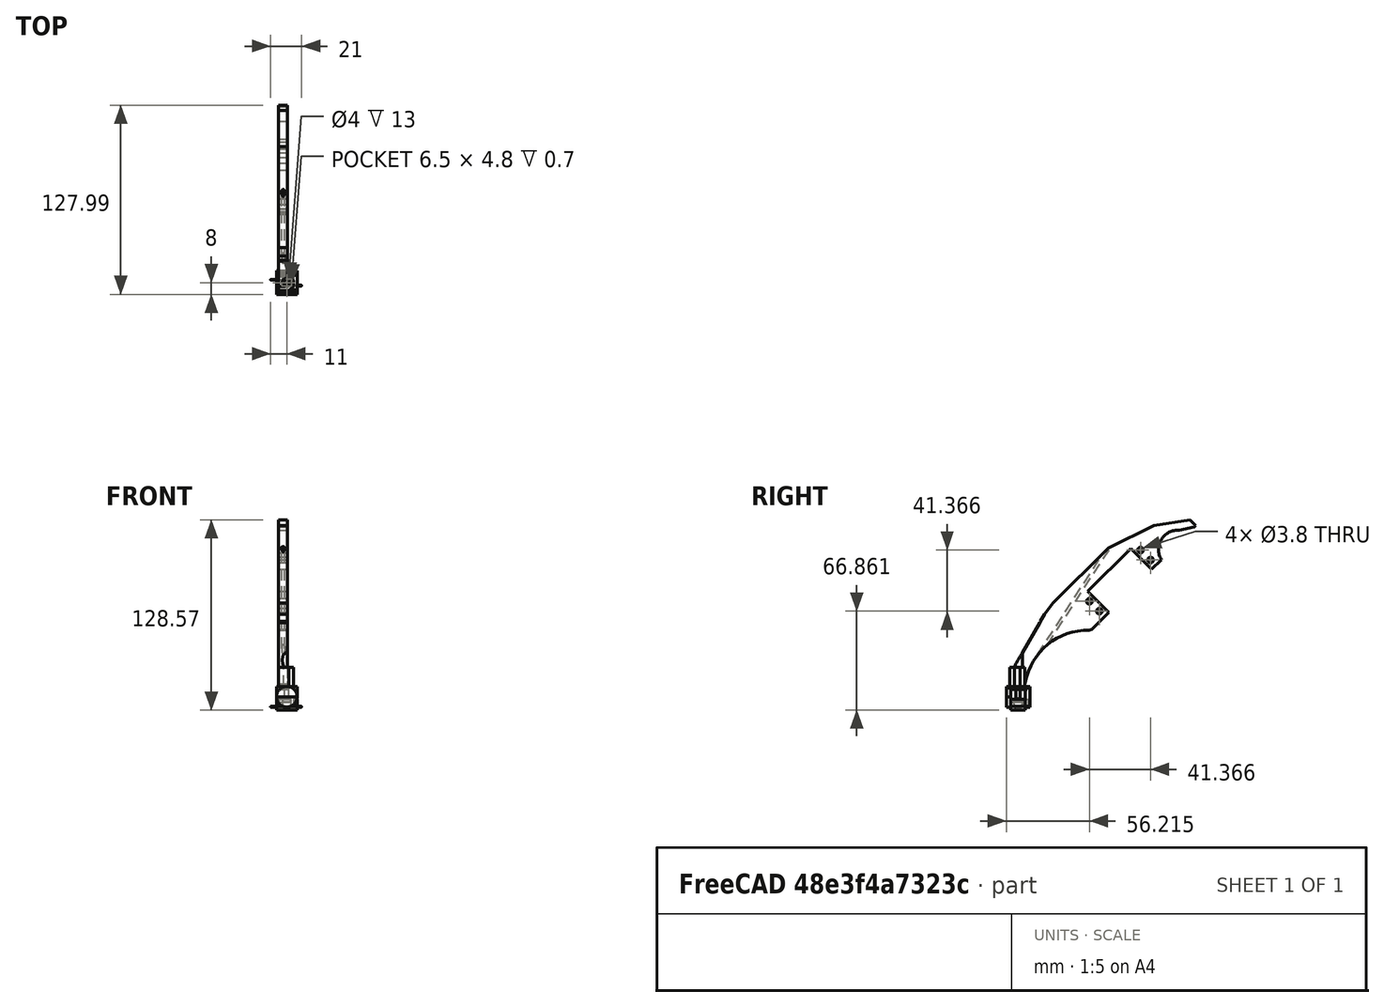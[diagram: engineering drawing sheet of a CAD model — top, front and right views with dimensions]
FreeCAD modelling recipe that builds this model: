
FCSTD DOCUMENT  (FreeCAD 0.16R6710 (Git))
Label: Leg and feet sensors 0.1
License: All rights reserved
LicenseURL: http://en.wikipedia.org/wiki/All_rights_reserved
objects: Part::Cut×27, Part::Box×24, Part::Cylinder×18, Part::Fuse×8, Part::Chamfer×4, Part::Sphere×2, Part::Fillet×2, Part::MultiCommon×1
note: 86 computed .brp shape members not serialized (recipe doc carries the construction recipe); baked Part::Feature solids carry a one-line shape summary decoded from their .brp

FEATURE [Part::Sphere] Sphere
  Angle1 = -90
  Angle2 = 90
  Angle3 = 360
  Radius = 3
FEATURE [Part::Cylinder] Cylinder
  Angle = 360
  Height = 10
  Radius = 1.5
FEATURE [Part::Box] Box  label="Cube"
  Height = 1
  Length = 6.5
  Placement = pos=(-3.25,-2.4,-4.2) rot=(0,0,1;0rad)
  Width = 4.8
FEATURE [Part::Cylinder] Cylinder001
  Angle = 360
  Height = 10
  Placement = pos=(-11,2,-3.7) rot=(0,1,0;1.5708rad)
  Radius = 0.25
FEATURE [Part::Cylinder] Cylinder002
  Angle = 360
  Height = 10
  Placement = pos=(0,-2,-3.7) rot=(0,1,0;1.5708rad)
  Radius = 0.25
FEATURE [Part::Box] Box001  label="Cube001"
  Height = 7.25
  Length = 14
  Placement = pos=(-7,-5,-6) rot=(0,0,1;0rad)
  Width = 10
FEATURE [Part::Box] Box002  label="Cube002"
  Height = 1
  Length = 6.5
  Placement = pos=(-3.25,-2.4,-4.2) rot=(0,0,1;0rad)
  Width = 4.8
FEATURE [Part::Cylinder] Cylinder003
  Angle = 360
  Height = 10
  Placement = pos=(-11,2,-3.7) rot=(0,1,0;1.5708rad)
  Radius = 0.25
FEATURE [Part::Cylinder] Cylinder004
  Angle = 360
  Height = 10
  Placement = pos=(0,-2,-3.7) rot=(0,1,0;1.5708rad)
  Radius = 0.25
FEATURE [Part::Fuse] Fusion
  Base = -> Cylinder003
  Tool = -> Cylinder004
FEATURE [Part::Fuse] Fusion001
  Base = -> Box002
  Tool = -> Fusion
FEATURE [Part::Box] Box003  label="Cube003"
  Height = 3
  Length = 10
  Placement = pos=(-5,-6,-3.5) rot=(0,0,1;0rad)
  Width = 12
FEATURE [Part::Cut] Cut
  Base = -> Box001
  Tool = -> Box003
FEATURE [Part::Cut] Cut001
  Base = -> Cut
  Tool = -> Fusion001
FEATURE [Part::Fuse] Fusion002
  Base = -> Cylinder001
  Tool = -> Cylinder002
FEATURE [Part::Fuse] Fusion003  label="Switch"
  Base = -> Box
  Tool = -> Fusion002
FEATURE [Part::Box] Box004  label="Cube004"
  Height = 5
  Length = 10
  Placement = pos=(-5,4,-3.55) rot=(0,0,1;0rad)
  Width = 3
FEATURE [Part::Sphere] Sphere001
  Angle1 = -90
  Angle2 = 90
  Angle3 = 360
  Radius = 3.1
FEATURE [Part::Cylinder] Cylinder005
  Angle = 360
  Height = 10
  Placement = pos=(0,0,0.5) rot=(0,0,1;0rad)
  Radius = 2.5
FEATURE [Part::Fuse] Fusion004
  Base = -> Sphere001
  Tool = -> Cylinder005
FEATURE [Part::Cut] Cut002
  Base = -> Cut001
  Tool = -> Fusion004
FEATURE [Part::Fuse] Fusion005  label="Ball and Screw"
  Base = -> Sphere
  Placement = pos=(0,0,-1) rot=(0,0,1;0rad)
  Tool = -> Cylinder
FEATURE [Part::Cut] Cut003
  Base = -> Cut001
  Tool = -> Fusion004
FEATURE [Part::Box] Box005  label="Cube005"
  Height = 8
  Length = 21
  Placement = pos=(-9,-7,-3.5) rot=(0,0,1;0rad)
  Width = 17
FEATURE [Part::Box] Box006  label="Cube006"
  Height = 12
  Length = 21
  Placement = pos=(-9,-7,-3.5) rot=(0,0,1;0rad)
  Width = 17
FEATURE [Part::Cut] Cut004  label="Bottom Switch holder"
  Base = -> Cut003
  Tool = -> Box005
FEATURE [Part::MultiCommon] Common  label="Ball and screw holder"
  Shapes = -> [Cut002,Box006]
FEATURE [Part::Box] Box007  label="Cube007"
  Height = 7
  Length = 14
  Placement = pos=(-7,5,3) rot=(0,0,1;0rad)
  Width = 3
FEATURE [Part::Cylinder] Cylinder006
  Angle = 360
  Height = 3
  Placement = pos=(0,8,3) rot=(1,0,0;1.5708rad)
  Radius = 7
FEATURE [Part::Fuse] Fusion006
  Base = -> Box007
  Tool = -> Cylinder006
FEATURE [Part::Box] Box008  label="Cube008"
  Height = 7
  Length = 14
  Placement = pos=(-7,-8,3) rot=(0,0,1;0rad)
  Width = 3
FEATURE [Part::Cylinder] Cylinder007
  Angle = 360
  Height = 3
  Placement = pos=(0,-5,3) rot=(1,0,0;1.5708rad)
  Radius = 7
FEATURE [Part::Box] Box009  label="Cube009"
  Height = 2
  Length = 14
  Placement = pos=(-7,-6,8) rot=(0,0,1;0rad)
  Width = 12
FEATURE [Part::Box] Box010  label="Cube010"
  Height = 12
  Length = 41
  Placement = pos=(42,14,-1) rot=(0,0,1;0rad)
  Width = 20
FEATURE [Part::Cylinder] Cylinder011
  Angle = 360
  Height = 12
  Placement = pos=(38,19.5,-1) rot=(0,0,1;0rad)
  Radius = 1.9
FEATURE [Part::Cylinder] Cylinder012
  Angle = 360
  Height = 12
  Placement = pos=(38,29,-1) rot=(0,0,1;0rad)
  Radius = 1.9
FEATURE [Part::Cylinder] Cylinder013
  Angle = 360
  Height = 12
  Placement = pos=(87,29,-1) rot=(0,0,1;0rad)
  Radius = 1.9
FEATURE [Part::Cylinder] Cylinder014
  Angle = 360
  Height = 12
  Placement = pos=(87,19.5,-1) rot=(0,0,1;0rad)
  Radius = 1.9
FEATURE [Part::Box] Box011  label="Cube011"
  Height = 6
  Length = 184
  Width = 34
FEATURE [Part::Box] Box012  label="Cube012"
  Height = 12
  Length = 37
  Width = 8
FEATURE [Part::Cylinder] Cylinder015
  Angle = 360
  Height = 10
  Placement = pos=(20,37,0) rot=(0,0,1;0rad)
  Radius = 13
FEATURE [Part::Cut] Cut008
  Base = -> Box011
  Tool = -> Box012
FEATURE [Part::Cut] Cut009
  Base = -> Cut008
  Tool = -> Cylinder015
FEATURE [Part::Cylinder] Cylinder016
  Angle = 360
  Height = 10
  Placement = pos=(132,63,0) rot=(0,0,1;0rad)
  Radius = 43
FEATURE [Part::Cut] Cut010
  Base = -> Cut009
  Tool = -> Cylinder016
FEATURE [Part::Box] Box013  label="Cube013"
  Height = 10
  Length = 41
  Placement = pos=(120,0,0) rot=(0,0,1;0rad)
  Width = 6
FEATURE [Part::Cut] Cut011
  Base = -> Cut010
  Tool = -> Box013
FEATURE [Part::Box] Box014  label="Cube014"
  Height = 10
  Length = 23
  Placement = pos=(161,0,0) rot=(0,0,1;0rad)
  Width = 17
FEATURE [Part::Cut] Cut012
  Base = -> Cut011
  Tool = -> Box014
FEATURE [Part::Box] Box015  label="Cube015"
  Height = 10
  Length = 13
  Placement = pos=(0,8,0) rot=(0,0,1;0rad)
  Width = 11
FEATURE [Part::Cut] Cut013
  Base = -> Cut012
  Tool = -> Box015
FEATURE [Part::Box] Box016  label="Cube016"
  Height = 10
  Length = 53
  Placement = pos=(-16,28,0) rot=(0,0,-1;0.628319rad)
  Width = 10
FEATURE [Part::Cut] Cut014
  Base = -> Cut013
  Tool = -> Box016
FEATURE [Part::Box] Box017  label="Cube017"
  Height = 10
  Length = 49
  Placement = pos=(16,5,0) rot=(0,0,-1;0.331613rad)
  Width = 10
FEATURE [Part::Cut] Cut015
  Base = -> Cut014
  Tool = -> Box017
FEATURE [Part::Box] Box018  label="Cube018"
  Height = 10
  Length = 76
  Placement = pos=(46,-7,0) rot=(0,0,1;0rad)
  Width = 10
FEATURE [Part::Cut] Cut016
  Base = -> Cut015
  Tool = -> Box018
FEATURE [Part::Box] Box019  label="Cube019"
  Height = 10
  Length = 65
  Placement = pos=(115,-7,0) rot=(0,0,1;0.261799rad)
  Width = 11
FEATURE [Part::Cut] Cut017
  Base = -> Cut016
  Tool = -> Box019
FEATURE [Part::Box] Box020  label="Cube020"
  Height = 10
  Length = 14
  Placement = pos=(174,10,0) rot=(0,0,1;0.279253rad)
  Width = 10
FEATURE [Part::Cut] Cut018
  Base = -> Cut017
  Tool = -> Box020
FEATURE [Part::Box] Box021  label="Cube021"
  Height = 10
  Length = 10
  Placement = pos=(106,-7,0) rot=(0,0,1;0.139626rad)
  Width = 10
FEATURE [Part::Cut] Cut019
  Base = -> Cut018
  Tool = -> Box021
FEATURE [Part::Cut] Cut020
  Base = -> Cut019
  Tool = -> Box010
FEATURE [Part::Cut] Cut021
  Base = -> Cut020
  Tool = -> Cylinder014
FEATURE [Part::Cut] Cut022
  Base = -> Cut021
  Tool = -> Cylinder013
FEATURE [Part::Cut] Cut023
  Base = -> Cut022
  Tool = -> Cylinder012
FEATURE [Part::Cut] Cut024
  Base = -> Cut023
  Tool = -> Cylinder011
FEATURE [Part::Chamfer] Chamfer
  Base = -> Cut024
  Edges = 1 edges r=6: [Edge36]
FEATURE [Part::Chamfer] Chamfer001
  Base = -> Chamfer
  Edges = 1 edges r=1: [Edge59]
FEATURE [Part::Box] Box022  label="Cube022"
  Height = 13
  Length = 26
  Placement = pos=(161,15,-3) rot=(0,0,1;0rad)
  Width = 23
FEATURE [Part::Cut] Cut025
  Base = -> Chamfer001
  Placement = pos=(-5.5,-24,171) rot=(0,1,0;1.5708rad)
  Tool = -> Box022
FEATURE [Part::Cylinder] Cylinder020
  Angle = 360
  Height = 16
  Placement = pos=(0,0,9) rot=(0,0,1;0rad)
  Radius = 2
FEATURE [Part::Fillet] Fillet
  Base = -> Cut025
  Edges = 1 edges r=3: [Edge30]
FEATURE [Part::Cylinder] Cylinder022  label="Not used cylinder001"
  Angle = 360
  Height = 16
  Placement = pos=(0,-50,23) rot=(0,0,1;0rad)
  Radius = 3
FEATURE [Part::Fillet] Fillet001
  Base = -> Fillet
  Edges = 1 edges r=3: [Edge39]
FEATURE [Part::Box] Box024  label="Cube024"
  Height = 13
  Length = 10
  Placement = pos=(-5.5,-5.5,10) rot=(0,0,1;0rad)
  Width = 10
FEATURE [Part::Cut] Cut035
  Base = -> Fillet001
  Placement = pos=(0,-8,5) rot=(-1,0,0;0.785398rad)
  Tool = -> Cylinder022
FEATURE [Part::Fuse] Fusion007
  Base = -> Box024
  Tool = -> Cut035
FEATURE [Part::Cylinder] Cylinder024
  Angle = 360
  Height = 16
  Placement = pos=(0,0,23) rot=(0,0,1;0rad)
  Radius = 3
FEATURE [Part::Cut] Cut036
  Base = -> Fusion007
  Tool = -> Cylinder024
FEATURE [Part::Cut] Cut037
  Base = -> Cut036
  Tool = -> Cylinder020
FEATURE [Part::Chamfer] Chamfer002
  Base = -> Cut037
  Edges = 1 edges r=3: [Edge13]
FEATURE [Part::Chamfer] Chamfer003
  Base = -> Chamfer002
  Edges = 1 edges r=3: [Edge21]
FEATURE [Part::Cylinder] Cylinder025
  Angle = 360
  Height = 96
  Placement = pos=(-2.5,14,31) rot=(-1,0,0;0.575959rad)
  Radius = 1
FEATURE [Part::Cut] Cut038  label="Leg"
  Base = -> Chamfer003
  Tool = -> Cylinder025
